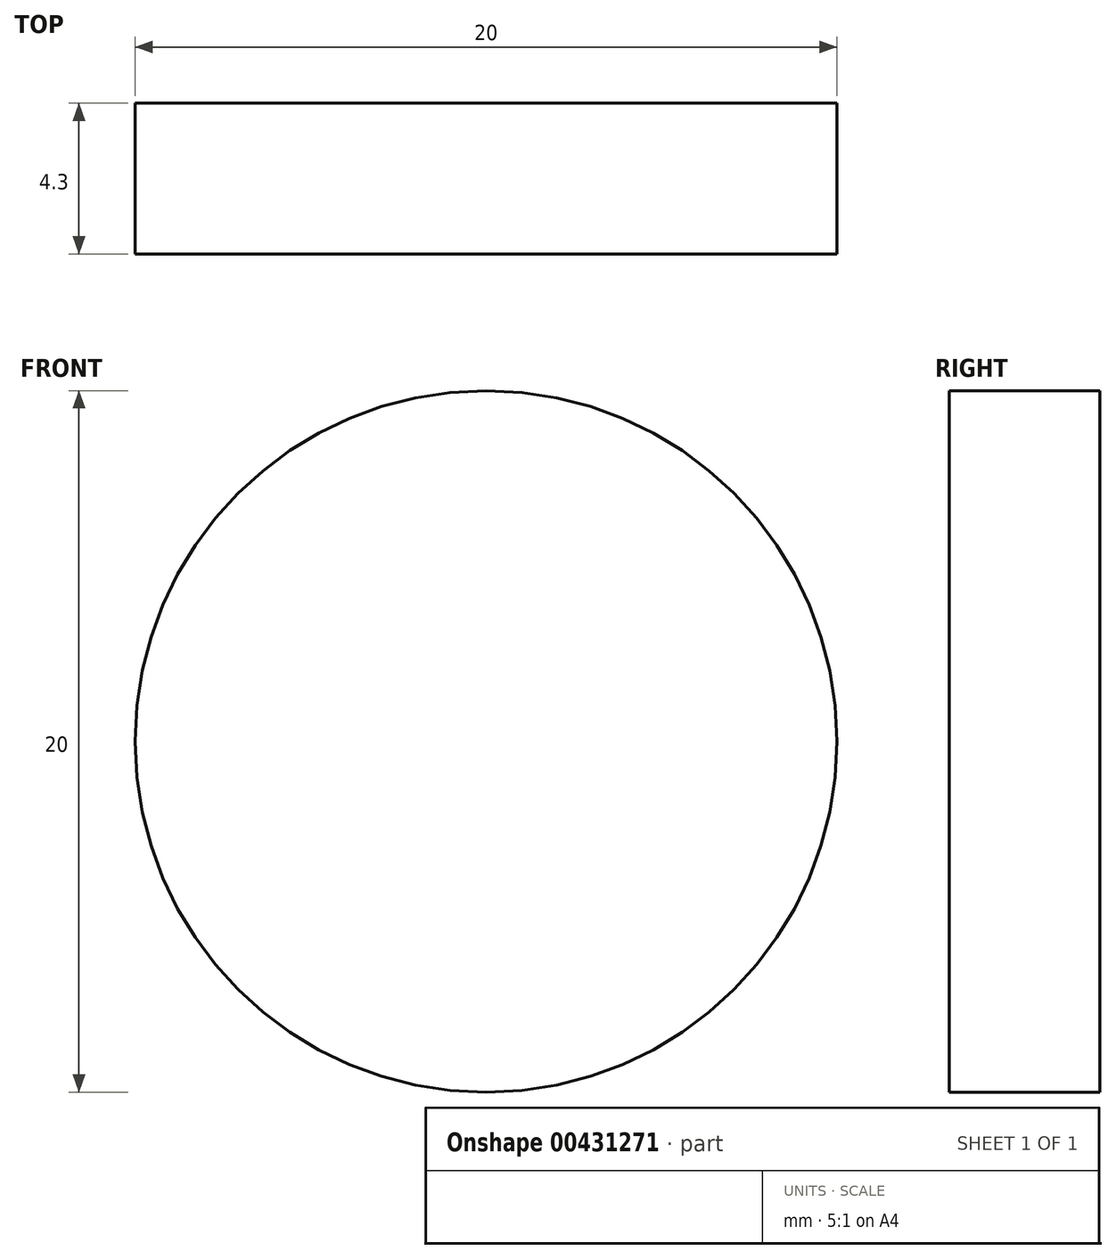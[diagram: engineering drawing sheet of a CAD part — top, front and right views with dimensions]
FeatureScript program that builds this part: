
annotation { "Feature Type Name" : "Feature", "Feature Type Description" : "" }
export const myFeature = defineFeature(function(context is Context, id is Id, definition is map)
    precondition{}
    {
        {
            var Q0;
            Q0=qCreatedBy(makeId("Front.planeOp"),FACE);
            var sketch = newSketch(context, id + "F0", { "sketchPlane" : qUnion([Q0])});
            skCircle(sketch, "E0", {"center": v(0, 0) * mm, "radius": 10 * mm});
            skSolve(sketch);
        }
        {
            var Q0;
            Q0 = qSketchRegion(id + "F0", true);
            var Q1;
            Q1=makeQuery(id+"F0.imprint","IMPRINT",FACE,{"disambiguationData":[TD([[makeQuery(id+"F0.imprint","IMPRINT",EDGE,{"derivedFrom":sQuery(id+"F0.wireOp",EDGE,"E0")}),1.0]])]});
            extrude(context, id + "F1", {"entities" : qUnion([Q0, Q1]), "depth" : 4.3 * mm});
        }
    });
